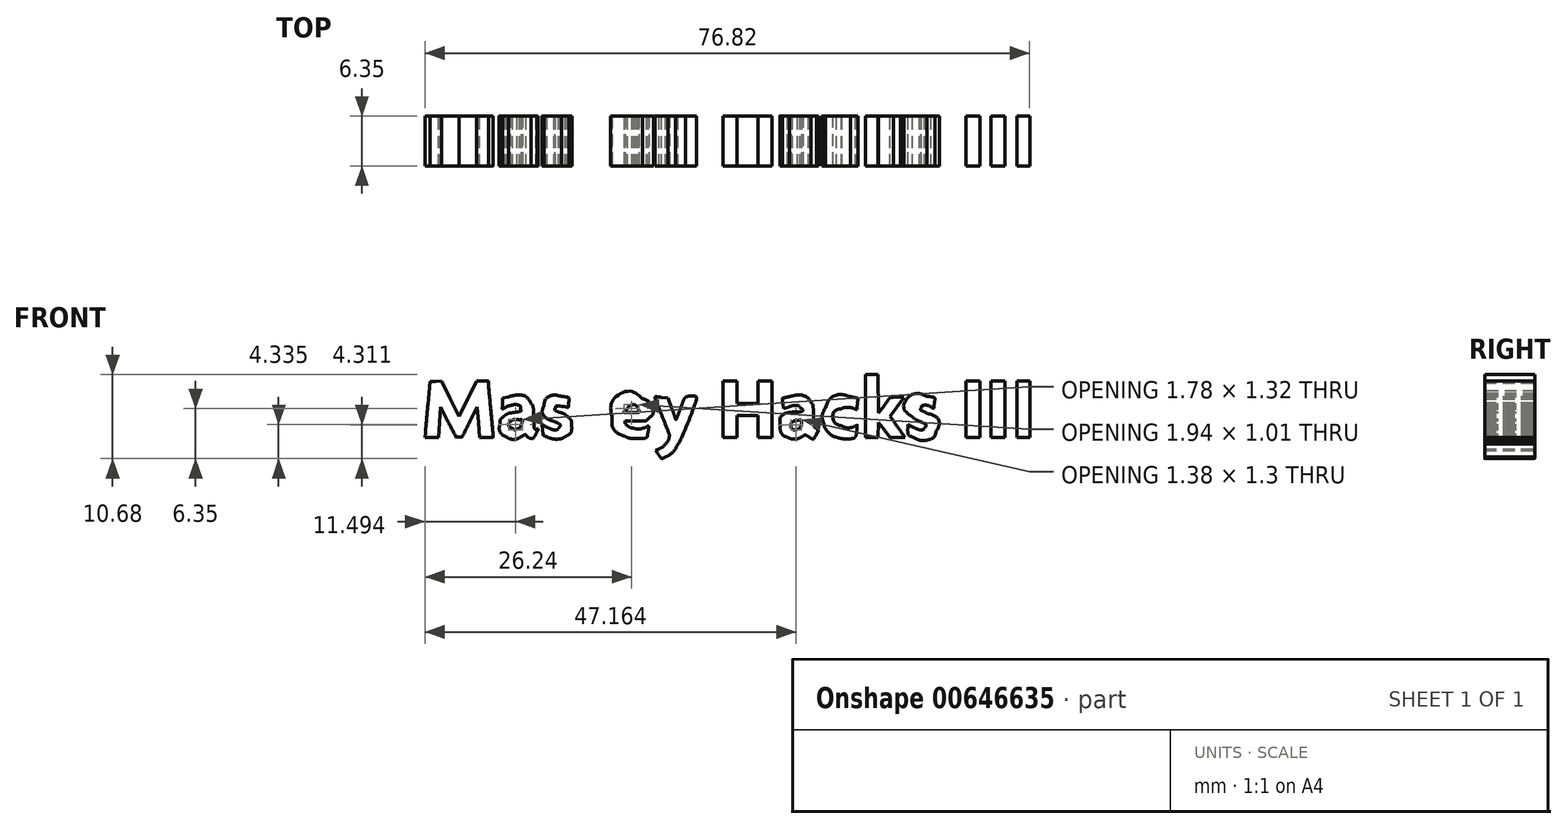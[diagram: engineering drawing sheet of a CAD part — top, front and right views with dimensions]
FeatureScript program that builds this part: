
annotation { "Feature Type Name" : "Feature", "Feature Type Description" : "" }
export const myFeature = defineFeature(function(context is Context, id is Id, definition is map)
    precondition{}
    {
        {
            var Q0;
            Q0=qCreatedBy(makeId("Front.planeOp"),FACE);
            var sketch = newSketch(context, id + "F0", { "sketchPlane" : qUnion([Q0])});
            skFitSpline(sketch, "E0", {"points": [v(-8.66, -4.08) * mm, v(-8.2, -3.84) * mm, v(-7.5, -3.03) * mm, v(-7.4, -2.6) * mm]});
            skFitSpline(sketch, "E1", {"points": [v(-7.4, -2.6) * mm, v(-7.35, -2.43) * mm, v(-7.66, -1.48) * mm, v(-8.27, 0.05) * mm]});
            skFitSpline(sketch, "E2", {"points": [v(-8.27, 0.05) * mm, v(-8.8, 1.37) * mm, v(-9.2, 2.47) * mm, v(-9.16, 2.5) * mm]});
            skFitSpline(sketch, "E3", {"points": [v(-9.16, 2.5) * mm, v(-9.13, 2.53) * mm, v(-8.76, 2.5) * mm, v(-8.33, 2.45) * mm]});
            skLineSegment(sketch, "E4", {"start": v(-8.74, -4.82) * mm, "end": v(-9.1, -4.3) * mm});
            skLineSegment(sketch, "E5", {"start": v(-9.1, -4.3) * mm, "end": v(-8.66, -4.08) * mm});
            skFitSpline(sketch, "E6", {"points": [v(-7.08, 1.11) * mm, v(-6.83, 0.44) * mm, v(-6.6, -0.2) * mm, v(-6.57, -0.3) * mm]});
            skFitSpline(sketch, "E7", {"points": [v(-6.57, -0.3) * mm, v(-6.53, -0.4) * mm, v(-6.27, 0.16) * mm, v(-6, 0.92) * mm]});
            skFitSpline(sketch, "E8", {"points": [v(-6, 0.92) * mm, v(-5.72, 1.7) * mm, v(-5.42, 2.36) * mm, v(-5.33, 2.42) * mm]});
            skFitSpline(sketch, "E9", {"points": [v(-5.33, 2.42) * mm, v(-5.09, 2.57) * mm, v(-3.94, 2.55) * mm, v(-3.94, 2.39) * mm]});
            skFitSpline(sketch, "E10", {"points": [v(-3.94, 2.39) * mm, v(-3.94, 2.14) * mm, v(-5.94, -2.92) * mm, v(-6.25, -3.46) * mm]});
            skFitSpline(sketch, "E11", {"points": [v(-6.25, -3.46) * mm, v(-6.65, -4.16) * mm, v(-7.3, -4.84) * mm, v(-7.83, -5.11) * mm]});
            skFitSpline(sketch, "E12", {"points": [v(-7.83, -5.11) * mm, v(-8.07, -5.24) * mm, v(-8.3, -5.34) * mm, v(-8.33, -5.34) * mm]});
            skFitSpline(sketch, "E13", {"points": [v(-8.33, -5.34) * mm, v(-8.36, -5.34) * mm, v(-8.55, -5.1) * mm, v(-8.74, -4.82) * mm]});
            skLineSegment(sketch, "E14", {"start": v(-8.33, 2.45) * mm, "end": v(-7.54, 2.35) * mm});
            skLineSegment(sketch, "E15", {"start": v(-7.54, 2.35) * mm, "end": v(-7.08, 1.11) * mm});
            skFitSpline(sketch, "E16", {"points": [v(-28.1, -2.54) * mm, v(-28.68, -2.24) * mm, v(-28.95, -1.68) * mm, v(-28.9, -0.94) * mm]});
            skFitSpline(sketch, "E17", {"points": [v(-28.9, -0.94) * mm, v(-28.85, -0.45) * mm, v(-28.78, -0.3) * mm, v(-28.4, 0.01) * mm]});
            skFitSpline(sketch, "E18", {"points": [v(-28.4, 0.01) * mm, v(-28.17, 0.22) * mm, v(-27.8, 0.41) * mm, v(-27.6, 0.45) * mm]});
            skFitSpline(sketch, "E19", {"points": [v(-27.6, 0.45) * mm, v(-27.4, 0.48) * mm, v(-27, 0.55) * mm, v(-26.72, 0.6) * mm]});
            skFitSpline(sketch, "E20", {"points": [v(-26.72, 0.6) * mm, v(-26.3, 0.66) * mm, v(-26.22, 0.7) * mm, v(-26.25, 0.92) * mm]});
            skFitSpline(sketch, "E21", {"points": [v(-26.25, 0.92) * mm, v(-26.32, 1.39) * mm, v(-27.44, 1.46) * mm, v(-28.38, 1.06) * mm]});
            skFitSpline(sketch, "E22", {"points": [v(-28.38, 1.06) * mm, v(-28.57, 0.98) * mm, v(-28.59, 1.03) * mm, v(-28.55, 1.65) * mm]});
            skFitSpline(sketch, "E23", {"points": [v(-27.81, 2.5) * mm, v(-26.54, 2.78) * mm, v(-25.5, 2.49) * mm, v(-24.9, 1.67) * mm]});
            skFitSpline(sketch, "E24", {"points": [v(-24.9, 1.67) * mm, v(-24.7, 1.41) * mm, v(-24.65, 1.1) * mm, v(-24.6, 0.03) * mm]});
            skFitSpline(sketch, "E25", {"points": [v(-24.6, 0.03) * mm, v(-24.53, -1.33) * mm, v(-24.46, -1.58) * mm, v(-24.17, -1.58) * mm]});
            skFitSpline(sketch, "E26", {"points": [v(-24.17, -1.58) * mm, v(-24.03, -1.58) * mm, v(-24.06, -1.71) * mm, v(-24.3, -2.17) * mm]});
            skFitSpline(sketch, "E27", {"points": [v(-24.3, -2.17) * mm, v(-24.46, -2.5) * mm, v(-24.67, -2.76) * mm, v(-24.77, -2.76) * mm]});
            skFitSpline(sketch, "E28", {"points": [v(-24.77, -2.76) * mm, v(-25, -2.76) * mm, v(-25.44, -2.53) * mm, v(-25.55, -2.36) * mm]});
            skFitSpline(sketch, "E29", {"points": [v(-25.55, -2.36) * mm, v(-25.6, -2.28) * mm, v(-25.79, -2.33) * mm, v(-26.1, -2.5) * mm]});
            skFitSpline(sketch, "E30", {"points": [v(-26.1, -2.5) * mm, v(-26.67, -2.82) * mm, v(-27.54, -2.84) * mm, v(-28.1, -2.54) * mm]});
            skLineSegment(sketch, "E31", {"start": v(-28.55, 1.65) * mm, "end": v(-28.52, 2.34) * mm});
            skLineSegment(sketch, "E32", {"start": v(-28.52, 2.34) * mm, "end": v(-27.81, 2.5) * mm});
            skFitSpline(sketch, "E33", {"points": [v(-26.22, -1.15) * mm, v(-26.03, -0.65) * mm, v(-26.08, -0.41) * mm, v(-26.39, -0.41) * mm]});
            skFitSpline(sketch, "E34", {"points": [v(-26.39, -0.41) * mm, v(-27.28, -0.41) * mm, v(-27.83, -1.05) * mm, v(-27.3, -1.48) * mm]});
            skFitSpline(sketch, "E35", {"points": [v(-27.3, -1.48) * mm, v(-27.09, -1.65) * mm, v(-26.98, -1.66) * mm, v(-26.69, -1.56) * mm]});
            skFitSpline(sketch, "E36", {"points": [v(-26.69, -1.56) * mm, v(-26.49, -1.5) * mm, v(-26.28, -1.31) * mm, v(-26.22, -1.15) * mm]});
            skFitSpline(sketch, "E37", {"points": [v(-22.87, -2.59) * mm, v(-23.11, -2.5) * mm, v(-23.33, -2.4) * mm, v(-23.35, -2.39) * mm]});
            skFitSpline(sketch, "E38", {"points": [v(-23.35, -2.39) * mm, v(-23.37, -2.36) * mm, v(-23.43, -2.04) * mm, v(-23.48, -1.66) * mm]});
            skFitSpline(sketch, "E39", {"points": [v(-23.08, -1.22) * mm, v(-22.4, -1.57) * mm, v(-21.63, -1.66) * mm, v(-21.43, -1.42) * mm]});
            skFitSpline(sketch, "E40", {"points": [v(-21.43, -1.42) * mm, v(-21.2, -1.13) * mm, v(-21.36, -0.9) * mm, v(-22.03, -0.6) * mm]});
            skFitSpline(sketch, "E41", {"points": [v(-22.03, -0.6) * mm, v(-23.08, -0.13) * mm, v(-23.51, 0.57) * mm, v(-23.28, 1.42) * mm]});
            skFitSpline(sketch, "E42", {"points": [v(-23.28, 1.42) * mm, v(-23.05, 2.26) * mm, v(-22.13, 2.74) * mm, v(-21.08, 2.58) * mm]});
            skFitSpline(sketch, "E43", {"points": [v(-21.08, 2.58) * mm, v(-20.21, 2.45) * mm, v(-20.11, 2.36) * mm, v(-20.15, 1.72) * mm]});
            skFitSpline(sketch, "E44", {"points": [v(-20.15, 1.72) * mm, v(-20.18, 1.3) * mm, v(-20.23, 1.18) * mm, v(-20.36, 1.22) * mm]});
            skFitSpline(sketch, "E45", {"points": [v(-20.36, 1.22) * mm, v(-20.46, 1.24) * mm, v(-20.8, 1.29) * mm, v(-21.14, 1.32) * mm]});
            skFitSpline(sketch, "E46", {"points": [v(-21.14, 1.32) * mm, v(-21.63, 1.37) * mm, v(-21.75, 1.34) * mm, v(-21.81, 1.17) * mm]});
            skFitSpline(sketch, "E47", {"points": [v(-21.81, 1.17) * mm, v(-21.92, 0.9) * mm, v(-21.74, 0.71) * mm, v(-21.16, 0.52) * mm]});
            skFitSpline(sketch, "E48", {"points": [v(-21.16, 0.52) * mm, v(-20.9, 0.43) * mm, v(-20.47, 0.17) * mm, v(-20.22, -0.07) * mm]});
            skFitSpline(sketch, "E49", {"points": [v(-20.22, -0.07) * mm, v(-19.83, -0.44) * mm, v(-19.78, -0.56) * mm, v(-19.78, -1.04) * mm]});
            skFitSpline(sketch, "E50", {"points": [v(-19.78, -1.04) * mm, v(-19.78, -1.77) * mm, v(-20.03, -2.23) * mm, v(-20.6, -2.52) * mm]});
            skFitSpline(sketch, "E51", {"points": [v(-20.6, -2.52) * mm, v(-21.14, -2.8) * mm, v(-22.18, -2.83) * mm, v(-22.87, -2.59) * mm]});
            skLineSegment(sketch, "E52", {"start": v(-23.48, -1.66) * mm, "end": v(-23.56, -0.98) * mm});
            skLineSegment(sketch, "E53", {"start": v(-23.56, -0.98) * mm, "end": v(-23.08, -1.22) * mm});
            skFitSpline(sketch, "E54", {"points": [v(-13.03, -2.48) * mm, v(-14.09, -1.98) * mm, v(-14.62, -1.16) * mm, v(-14.61, -0.03) * mm]});
            skFitSpline(sketch, "E55", {"points": [v(-14.61, -0.03) * mm, v(-14.6, 1.98) * mm, v(-12.5, 3.24) * mm, v(-10.74, 2.27) * mm]});
            skFitSpline(sketch, "E56", {"points": [v(-10.74, 2.27) * mm, v(-9.79, 1.74) * mm, v(-9.42, 0.43) * mm, v(-10.03, -0.23) * mm]});
            skFitSpline(sketch, "E57", {"points": [v(-10.03, -0.23) * mm, v(-10.3, -0.52) * mm, v(-10.37, -0.53) * mm, v(-11.64, -0.53) * mm]});
            skFitSpline(sketch, "E58", {"points": [v(-11.64, -0.53) * mm, v(-12.37, -0.53) * mm, v(-12.97, -0.57) * mm, v(-12.97, -0.63) * mm]});
            skFitSpline(sketch, "E59", {"points": [v(-12.97, -0.63) * mm, v(-12.97, -0.86) * mm, v(-12.38, -1.34) * mm, v(-11.94, -1.46) * mm]});
            skFitSpline(sketch, "E60", {"points": [v(-11.94, -1.46) * mm, v(-11.5, -1.58) * mm, v(-10.83, -1.51) * mm, v(-10.24, -1.28) * mm]});
            skFitSpline(sketch, "E61", {"points": [v(-10.24, -1.28) * mm, v(-10.02, -1.2) * mm, v(-9.98, -1.48) * mm, v(-10.11, -2.15) * mm]});
            skFitSpline(sketch, "E62", {"points": [v(-10.11, -2.15) * mm, v(-10.2, -2.6) * mm, v(-10.6, -2.76) * mm, v(-11.67, -2.76) * mm]});
            skFitSpline(sketch, "E63", {"points": [v(-11.67, -2.76) * mm, v(-12.24, -2.76) * mm, v(-12.6, -2.68) * mm, v(-13.03, -2.48) * mm]});
            skFitSpline(sketch, "E64", {"points": [v(-11.21, 0.68) * mm, v(-11.21, 0.76) * mm, v(-11.3, 0.95) * mm, v(-11.4, 1.09) * mm]});
            skFitSpline(sketch, "E65", {"points": [v(-11.4, 1.09) * mm, v(-11.65, 1.46) * mm, v(-12.3, 1.44) * mm, v(-12.68, 1.06) * mm]});
            skFitSpline(sketch, "E66", {"points": [v(-12.68, 1.06) * mm, v(-13.14, 0.6) * mm, v(-13.05, 0.53) * mm, v(-12.1, 0.53) * mm]});
            skFitSpline(sketch, "E67", {"points": [v(-12.1, 0.53) * mm, v(-11.46, 0.53) * mm, v(-11.21, 0.57) * mm, v(-11.21, 0.68) * mm]});
            skFitSpline(sketch, "E68", {"points": [v(7.6, -2.58) * mm, v(7.09, -2.36) * mm, v(6.74, -1.77) * mm, v(6.74, -1.13) * mm]});
            skFitSpline(sketch, "E69", {"points": [v(6.74, -1.13) * mm, v(6.74, -0.14) * mm, v(7.4, 0.43) * mm, v(8.76, 0.58) * mm]});
            skFitSpline(sketch, "E70", {"points": [v(8.76, 0.58) * mm, v(9.47, 0.67) * mm, v(9.6, 0.82) * mm, v(9.25, 1.16) * mm]});
            skFitSpline(sketch, "E71", {"points": [v(9.25, 1.16) * mm, v(9.02, 1.4) * mm, v(8.36, 1.4) * mm, v(7.65, 1.19) * mm]});
            skFitSpline(sketch, "E72", {"points": [v(7.06, 1.63) * mm, v(7, 2.32) * mm, v(7.01, 2.35) * mm, v(7.9, 2.53) * mm]});
            skFitSpline(sketch, "E73", {"points": [v(7.9, 2.53) * mm, v(9.02, 2.77) * mm, v(10.15, 2.46) * mm, v(10.66, 1.78) * mm]});
            skFitSpline(sketch, "E74", {"points": [v(10.66, 1.78) * mm, v(10.86, 1.51) * mm, v(10.9, 1.22) * mm, v(10.96, 0.1) * mm]});
            skFitSpline(sketch, "E75", {"points": [v(10.96, 0.1) * mm, v(11.02, -1.15) * mm, v(11.05, -1.28) * mm, v(11.3, -1.49) * mm]});
            skLineSegment(sketch, "E76", {"start": v(7.65, 1.19) * mm, "end": v(7.12, 1.03) * mm});
            skLineSegment(sketch, "E77", {"start": v(7.12, 1.03) * mm, "end": v(7.06, 1.63) * mm});
            skFitSpline(sketch, "E78", {"points": [v(11.3, -2.24) * mm, v(11, -2.82) * mm, v(10.84, -2.86) * mm, v(10.3, -2.53) * mm]});
            skFitSpline(sketch, "E79", {"points": [v(10.3, -2.53) * mm, v(9.93, -2.3) * mm, v(9.92, -2.3) * mm, v(9.48, -2.53) * mm]});
            skFitSpline(sketch, "E80", {"points": [v(9.48, -2.53) * mm, v(8.96, -2.8) * mm, v(8.13, -2.82) * mm, v(7.6, -2.58) * mm]});
            skLineSegment(sketch, "E81", {"start": v(11.3, -1.49) * mm, "end": v(11.6, -1.72) * mm});
            skLineSegment(sketch, "E82", {"start": v(11.6, -1.72) * mm, "end": v(11.3, -2.24) * mm});
            skLineSegment(sketch, "E83", {"start": v(11.3, -2.24) * mm, "end": v(11.3, -1.49) * mm});
            skFitSpline(sketch, "E84", {"points": [v(9.22, -1.39) * mm, v(9.35, -1.27) * mm, v(9.44, -1.03) * mm, v(9.44, -0.79) * mm]});
            skLineSegment(sketch, "E85", {"start": v(7.6, -2.58) * mm, "end": v(7.6, -2.58) * mm});
            skFitSpline(sketch, "E86", {"points": [v(8.94, -0.46) * mm, v(8.67, -0.5) * mm, v(8.38, -0.6) * mm, v(8.3, -0.66) * mm]});
            skFitSpline(sketch, "E87", {"points": [v(8.3, -0.66) * mm, v(8.14, -0.8) * mm, v(8.09, -1.37) * mm, v(8.22, -1.5) * mm]});
            skFitSpline(sketch, "E88", {"points": [v(8.22, -1.5) * mm, v(8.37, -1.66) * mm, v(9, -1.58) * mm, v(9.22, -1.39) * mm]});
            skLineSegment(sketch, "E89", {"start": v(9.44, -0.79) * mm, "end": v(9.44, -0.38) * mm});
            skLineSegment(sketch, "E90", {"start": v(9.44, -0.38) * mm, "end": v(8.94, -0.46) * mm});
            skFitSpline(sketch, "E91", {"points": [v(13.9, -2.6) * mm, v(13.32, -2.42) * mm, v(12.42, -1.48) * mm, v(12.26, -0.92) * mm]});
            skFitSpline(sketch, "E92", {"points": [v(12.26, -0.92) * mm, v(12.05, -0.17) * mm, v(12.1, 0.44) * mm, v(12.46, 1.12) * mm]});
            skFitSpline(sketch, "E93", {"points": [v(12.46, 1.12) * mm, v(13.03, 2.26) * mm, v(14.3, 2.82) * mm, v(15.66, 2.53) * mm]});
            skFitSpline(sketch, "E94", {"points": [v(15.66, 2.53) * mm, v(16.58, 2.34) * mm, v(16.6, 2.32) * mm, v(16.51, 1.55) * mm]});
            skFitSpline(sketch, "E95", {"points": [v(16.51, 1.55) * mm, v(16.45, 0.98) * mm, v(16.4, 0.88) * mm, v(16.25, 0.95) * mm]});
            skFitSpline(sketch, "E96", {"points": [v(16.25, 0.95) * mm, v(15.86, 1.11) * mm, v(14.83, 1.14) * mm, v(14.48, 1) * mm]});
            skFitSpline(sketch, "E97", {"points": [v(14.48, 1) * mm, v(13.54, 0.6) * mm, v(13.58, -0.71) * mm, v(14.55, -1.17) * mm]});
            skFitSpline(sketch, "E98", {"points": [v(14.55, -1.17) * mm, v(14.98, -1.38) * mm, v(15.79, -1.38) * mm, v(16.29, -1.17) * mm]});
            skFitSpline(sketch, "E99", {"points": [v(16.29, -1.17) * mm, v(16.5, -1.08) * mm, v(16.5, -1.12) * mm, v(16.44, -1.76) * mm]});
            skFitSpline(sketch, "E100", {"points": [v(16.44, -1.76) * mm, v(16.4, -2.13) * mm, v(16.32, -2.5) * mm, v(16.25, -2.56) * mm]});
            skFitSpline(sketch, "E101", {"points": [v(16.25, -2.56) * mm, v(16.08, -2.73) * mm, v(14.37, -2.77) * mm, v(13.9, -2.6) * mm]});
            skFitSpline(sketch, "E102", {"points": [v(23.5, -2.57) * mm, v(23.07, -2.39) * mm, v(22.93, -2.08) * mm, v(22.93, -1.27) * mm]});
            skLineSegment(sketch, "E103", {"start": v(13.9, -2.6) * mm, "end": v(13.9, -2.6) * mm});
            skFitSpline(sketch, "E104", {"points": [v(23.54, -1.3) * mm, v(24.24, -1.62) * mm, v(24.83, -1.67) * mm, v(25.04, -1.4) * mm]});
            skFitSpline(sketch, "E105", {"points": [v(25.04, -1.4) * mm, v(25.27, -1.13) * mm, v(25.1, -0.9) * mm, v(24.43, -0.6) * mm]});
            skFitSpline(sketch, "E106", {"points": [v(24.43, -0.6) * mm, v(24.09, -0.45) * mm, v(23.7, -0.2) * mm, v(23.55, -0.05) * mm]});
            skFitSpline(sketch, "E107", {"points": [v(23.55, -0.05) * mm, v(22.4, 1.2) * mm, v(23.55, 2.85) * mm, v(25.38, 2.58) * mm]});
            skFitSpline(sketch, "E108", {"points": [v(25.38, 2.58) * mm, v(26.26, 2.45) * mm, v(26.37, 2.35) * mm, v(26.3, 1.74) * mm]});
            skFitSpline(sketch, "E109", {"points": [v(26.3, 1.74) * mm, v(26.23, 1.11) * mm, v(26.18, 1.06) * mm, v(25.88, 1.22) * mm]});
            skFitSpline(sketch, "E110", {"points": [v(25.88, 1.22) * mm, v(25.5, 1.42) * mm, v(24.73, 1.38) * mm, v(24.64, 1.16) * mm]});
            skFitSpline(sketch, "E111", {"points": [v(24.64, 1.16) * mm, v(24.53, 0.88) * mm, v(24.64, 0.79) * mm, v(25.46, 0.42) * mm]});
            skFitSpline(sketch, "E112", {"points": [v(25.46, 0.42) * mm, v(26.59, -0.1) * mm, v(26.94, -0.86) * mm, v(26.51, -1.88) * mm]});
            skFitSpline(sketch, "E113", {"points": [v(26.51, -1.88) * mm, v(26.19, -2.66) * mm, v(24.59, -3.02) * mm, v(23.5, -2.57) * mm]});
            skLineSegment(sketch, "E114", {"start": v(22.93, -1.27) * mm, "end": v(22.93, -1) * mm});
            skLineSegment(sketch, "E115", {"start": v(22.93, -1) * mm, "end": v(23.54, -1.3) * mm});
            skFitSpline(sketch, "E116", {"points": [v(-38.35, -2.02) * mm, v(-38.32, -1.69) * mm, v(-38.18, -0.09) * mm, v(-38.04, 1.53) * mm]});
            skLineSegment(sketch, "E117", {"start": v(23.5, -2.57) * mm, "end": v(23.5, -2.57) * mm});
            skFitSpline(sketch, "E118", {"points": [v(-31.09, 4.52) * mm, v(-30.39, 4.52) * mm, v(-30.34, 4.5) * mm, v(-30.33, 4.25) * mm]});
            skFitSpline(sketch, "E119", {"points": [v(-30.33, 4.25) * mm, v(-30.33, 4.1) * mm, v(-30.2, 2.59) * mm, v(-30.04, 0.88) * mm]});
            skFitSpline(sketch, "E120", {"points": [v(-30.04, 0.88) * mm, v(-29.88, -0.83) * mm, v(-29.75, -2.32) * mm, v(-29.75, -2.43) * mm]});
            skFitSpline(sketch, "E121", {"points": [v(-29.75, -2.43) * mm, v(-29.75, -2.61) * mm, v(-29.87, -2.64) * mm, v(-30.6, -2.64) * mm]});
            skLineSegment(sketch, "E122", {"start": v(-38.04, 1.53) * mm, "end": v(-37.79, 4.46) * mm});
            skLineSegment(sketch, "E123", {"start": v(-37.79, 4.46) * mm, "end": v(-37.06, 4.5) * mm});
            skLineSegment(sketch, "E124", {"start": v(-37.06, 4.5) * mm, "end": v(-36.33, 4.53) * mm});
            skLineSegment(sketch, "E125", {"start": v(-36.33, 4.53) * mm, "end": v(-35.2, 2.28) * mm});
            skLineSegment(sketch, "E126", {"start": v(-35.2, 2.28) * mm, "end": v(-34.08, 0.04) * mm});
            skLineSegment(sketch, "E127", {"start": v(-34.08, 0.04) * mm, "end": v(-32.96, 2.28) * mm});
            skLineSegment(sketch, "E128", {"start": v(-32.96, 2.28) * mm, "end": v(-31.84, 4.52) * mm});
            skLineSegment(sketch, "E129", {"start": v(-31.84, 4.52) * mm, "end": v(-31.09, 4.52) * mm});
            skFitSpline(sketch, "E130", {"points": [v(-32.73, -0.68) * mm, v(-33.68, -2.57) * mm, v(-33.68, -2.58) * mm, v(-34.08, -2.58) * mm]});
            skFitSpline(sketch, "E131", {"points": [v(-34.08, -2.58) * mm, v(-34.47, -2.58) * mm, v(-34.48, -2.57) * mm, v(-35.44, -0.68) * mm]});
            skLineSegment(sketch, "E132", {"start": v(-30.6, -2.64) * mm, "end": v(-31.47, -2.64) * mm});
            skLineSegment(sketch, "E133", {"start": v(-31.47, -2.64) * mm, "end": v(-31.62, -0.71) * mm});
            skLineSegment(sketch, "E134", {"start": v(-31.62, -0.71) * mm, "end": v(-31.77, 1.22) * mm});
            skLineSegment(sketch, "E135", {"start": v(-31.77, 1.22) * mm, "end": v(-32.73, -0.68) * mm});
            skLineSegment(sketch, "E136", {"start": v(-35.44, -0.68) * mm, "end": v(-36.4, 1.23) * mm});
            skLineSegment(sketch, "E137", {"start": v(-36.4, 1.23) * mm, "end": v(-36.55, -0.7) * mm});
            skLineSegment(sketch, "E138", {"start": v(-36.55, -0.7) * mm, "end": v(-36.7, -2.64) * mm});
            skLineSegment(sketch, "E139", {"start": v(-36.7, -2.64) * mm, "end": v(-37.56, -2.64) * mm});
            skLineSegment(sketch, "E140", {"start": v(-37.56, -2.64) * mm, "end": v(-38.41, -2.64) * mm});
            skLineSegment(sketch, "E141", {"start": v(-38.41, -2.64) * mm, "end": v(-38.35, -2.02) * mm});
            skLineSegment(sketch, "E142", {"start": v(-0.54, 0.94) * mm, "end": v(-0.54, 4.52) * mm});
            skLineSegment(sketch, "E143", {"start": v(-0.54, 4.52) * mm, "end": v(0.34, 4.52) * mm});
            skLineSegment(sketch, "E144", {"start": v(0.34, 4.52) * mm, "end": v(1.22, 4.52) * mm});
            skLineSegment(sketch, "E145", {"start": v(1.22, 4.52) * mm, "end": v(1.22, 3.1) * mm});
            skLineSegment(sketch, "E146", {"start": v(1.22, 3.1) * mm, "end": v(1.22, 1.7) * mm});
            skLineSegment(sketch, "E147", {"start": v(1.22, 1.7) * mm, "end": v(2.57, 1.7) * mm});
            skLineSegment(sketch, "E148", {"start": v(2.57, 1.7) * mm, "end": v(3.92, 1.7) * mm});
            skLineSegment(sketch, "E149", {"start": v(3.92, 1.7) * mm, "end": v(3.92, 3.1) * mm});
            skLineSegment(sketch, "E150", {"start": v(3.92, 3.1) * mm, "end": v(3.92, 4.52) * mm});
            skLineSegment(sketch, "E151", {"start": v(3.92, 4.52) * mm, "end": v(4.8, 4.52) * mm});
            skLineSegment(sketch, "E152", {"start": v(4.8, 4.52) * mm, "end": v(5.68, 4.52) * mm});
            skLineSegment(sketch, "E153", {"start": v(5.68, 4.52) * mm, "end": v(5.68, 0.94) * mm});
            skLineSegment(sketch, "E154", {"start": v(5.68, 0.94) * mm, "end": v(5.68, -2.64) * mm});
            skLineSegment(sketch, "E155", {"start": v(5.68, -2.64) * mm, "end": v(4.8, -2.64) * mm});
            skLineSegment(sketch, "E156", {"start": v(4.8, -2.64) * mm, "end": v(3.92, -2.64) * mm});
            skLineSegment(sketch, "E157", {"start": v(3.92, -2.64) * mm, "end": v(3.92, -1.23) * mm});
            skLineSegment(sketch, "E158", {"start": v(3.92, -1.23) * mm, "end": v(3.92, 0.18) * mm});
            skLineSegment(sketch, "E159", {"start": v(3.92, 0.18) * mm, "end": v(2.57, 0.18) * mm});
            skLineSegment(sketch, "E160", {"start": v(2.57, 0.18) * mm, "end": v(1.22, 0.18) * mm});
            skLineSegment(sketch, "E161", {"start": v(1.22, 0.18) * mm, "end": v(1.22, -1.23) * mm});
            skLineSegment(sketch, "E162", {"start": v(1.22, -1.23) * mm, "end": v(1.22, -2.64) * mm});
            skLineSegment(sketch, "E163", {"start": v(1.22, -2.64) * mm, "end": v(0.34, -2.64) * mm});
            skLineSegment(sketch, "E164", {"start": v(0.34, -2.64) * mm, "end": v(-0.54, -2.64) * mm});
            skLineSegment(sketch, "E165", {"start": v(-0.54, -2.64) * mm, "end": v(-0.54, 0.94) * mm});
            skFitSpline(sketch, "E166", {"points": [v(19.94, 1.45) * mm, v(20.57, 2.3) * mm, v(20.69, 2.4) * mm, v(21.1, 2.47) * mm]});
            skFitSpline(sketch, "E167", {"points": [v(21.1, 2.47) * mm, v(21.37, 2.5) * mm, v(21.77, 2.52) * mm, v(22.01, 2.5) * mm]});
            skLineSegment(sketch, "E168", {"start": v(17.53, 1.35) * mm, "end": v(17.53, 5.34) * mm});
            skLineSegment(sketch, "E169", {"start": v(17.53, 5.34) * mm, "end": v(18.35, 5.34) * mm});
            skLineSegment(sketch, "E170", {"start": v(18.35, 5.34) * mm, "end": v(19.17, 5.34) * mm});
            skLineSegment(sketch, "E171", {"start": v(19.17, 5.34) * mm, "end": v(19.2, 2.92) * mm});
            skLineSegment(sketch, "E172", {"start": v(19.2, 2.92) * mm, "end": v(19.23, 0.5) * mm});
            skLineSegment(sketch, "E173", {"start": v(19.23, 0.5) * mm, "end": v(19.94, 1.45) * mm});
            skFitSpline(sketch, "E174", {"points": [v(21.03, -0.45) * mm, v(21.23, -0.72) * mm, v(21.66, -1.32) * mm, v(21.99, -1.79) * mm]});
            skLineSegment(sketch, "E175", {"start": v(22.01, 2.5) * mm, "end": v(22.45, 2.46) * mm});
            skLineSegment(sketch, "E176", {"start": v(22.45, 2.46) * mm, "end": v(21.56, 1.25) * mm});
            skLineSegment(sketch, "E177", {"start": v(21.56, 1.25) * mm, "end": v(20.68, 0.03) * mm});
            skLineSegment(sketch, "E178", {"start": v(20.68, 0.03) * mm, "end": v(21.03, -0.45) * mm});
            skLineSegment(sketch, "E179", {"start": v(21.99, -1.79) * mm, "end": v(22.59, -2.64) * mm});
            skLineSegment(sketch, "E180", {"start": v(22.59, -2.64) * mm, "end": v(21.61, -2.64) * mm});
            skLineSegment(sketch, "E181", {"start": v(21.61, -2.64) * mm, "end": v(20.64, -2.63) * mm});
            skLineSegment(sketch, "E182", {"start": v(20.64, -2.63) * mm, "end": v(19.94, -1.67) * mm});
            skLineSegment(sketch, "E183", {"start": v(19.94, -1.67) * mm, "end": v(19.23, -0.71) * mm});
            skLineSegment(sketch, "E184", {"start": v(19.23, -0.71) * mm, "end": v(19.2, -1.68) * mm});
            skLineSegment(sketch, "E185", {"start": v(19.2, -1.68) * mm, "end": v(19.16, -2.64) * mm});
            skLineSegment(sketch, "E186", {"start": v(19.16, -2.64) * mm, "end": v(18.35, -2.64) * mm});
            skLineSegment(sketch, "E187", {"start": v(18.35, -2.64) * mm, "end": v(17.53, -2.64) * mm});
            skLineSegment(sketch, "E188", {"start": v(17.53, -2.64) * mm, "end": v(17.53, 1.35) * mm});
            skLineSegment(sketch, "E189", {"start": v(17.53, 1.35) * mm, "end": v(17.53, 1.35) * mm});
            skLineSegment(sketch, "E190", {"start": v(30.32, 0.94) * mm, "end": v(30.32, 4.52) * mm});
            skLineSegment(sketch, "E191", {"start": v(30.32, 4.52) * mm, "end": v(31.2, 4.52) * mm});
            skLineSegment(sketch, "E192", {"start": v(31.2, 4.52) * mm, "end": v(32.08, 4.52) * mm});
            skLineSegment(sketch, "E193", {"start": v(32.08, 4.52) * mm, "end": v(32.08, 0.94) * mm});
            skLineSegment(sketch, "E194", {"start": v(32.08, 0.94) * mm, "end": v(32.08, -2.64) * mm});
            skLineSegment(sketch, "E195", {"start": v(32.08, -2.64) * mm, "end": v(31.2, -2.64) * mm});
            skLineSegment(sketch, "E196", {"start": v(31.2, -2.64) * mm, "end": v(30.32, -2.64) * mm});
            skLineSegment(sketch, "E197", {"start": v(30.32, -2.64) * mm, "end": v(30.32, 0.94) * mm});
            skLineSegment(sketch, "E198", {"start": v(33.49, 0.94) * mm, "end": v(33.49, 4.52) * mm});
            skLineSegment(sketch, "E199", {"start": v(33.49, 4.52) * mm, "end": v(34.37, 4.52) * mm});
            skLineSegment(sketch, "E200", {"start": v(34.37, 4.52) * mm, "end": v(35.25, 4.52) * mm});
            skLineSegment(sketch, "E201", {"start": v(35.25, 4.52) * mm, "end": v(35.25, 0.94) * mm});
            skLineSegment(sketch, "E202", {"start": v(35.25, 0.94) * mm, "end": v(35.25, -2.64) * mm});
            skLineSegment(sketch, "E203", {"start": v(35.25, -2.64) * mm, "end": v(34.37, -2.64) * mm});
            skLineSegment(sketch, "E204", {"start": v(34.37, -2.64) * mm, "end": v(33.49, -2.64) * mm});
            skLineSegment(sketch, "E205", {"start": v(33.49, -2.64) * mm, "end": v(33.49, 0.94) * mm});
            skLineSegment(sketch, "E206", {"start": v(36.77, 0.94) * mm, "end": v(36.77, 4.52) * mm});
            skLineSegment(sketch, "E207", {"start": v(36.77, 4.52) * mm, "end": v(37.6, 4.52) * mm});
            skLineSegment(sketch, "E208", {"start": v(37.6, 4.52) * mm, "end": v(38.41, 4.52) * mm});
            skLineSegment(sketch, "E209", {"start": v(38.41, 4.52) * mm, "end": v(38.41, 0.94) * mm});
            skLineSegment(sketch, "E210", {"start": v(38.41, 0.94) * mm, "end": v(38.41, -2.64) * mm});
            skLineSegment(sketch, "E211", {"start": v(38.41, -2.64) * mm, "end": v(37.6, -2.64) * mm});
            skLineSegment(sketch, "E212", {"start": v(37.6, -2.64) * mm, "end": v(36.77, -2.64) * mm});
            skLineSegment(sketch, "E213", {"start": v(36.77, -2.64) * mm, "end": v(36.77, 0.94) * mm});
            skSolve(sketch);
        }
        {
            var Q0;
            Q0 = qSketchRegion(id + "F0", true);
            extrude(context, id + "F1", {"entities" : qUnion([Q0]), "depth" : 6.35 * mm, "offsetDistance" : 25.4 * mm});
        }
    });
